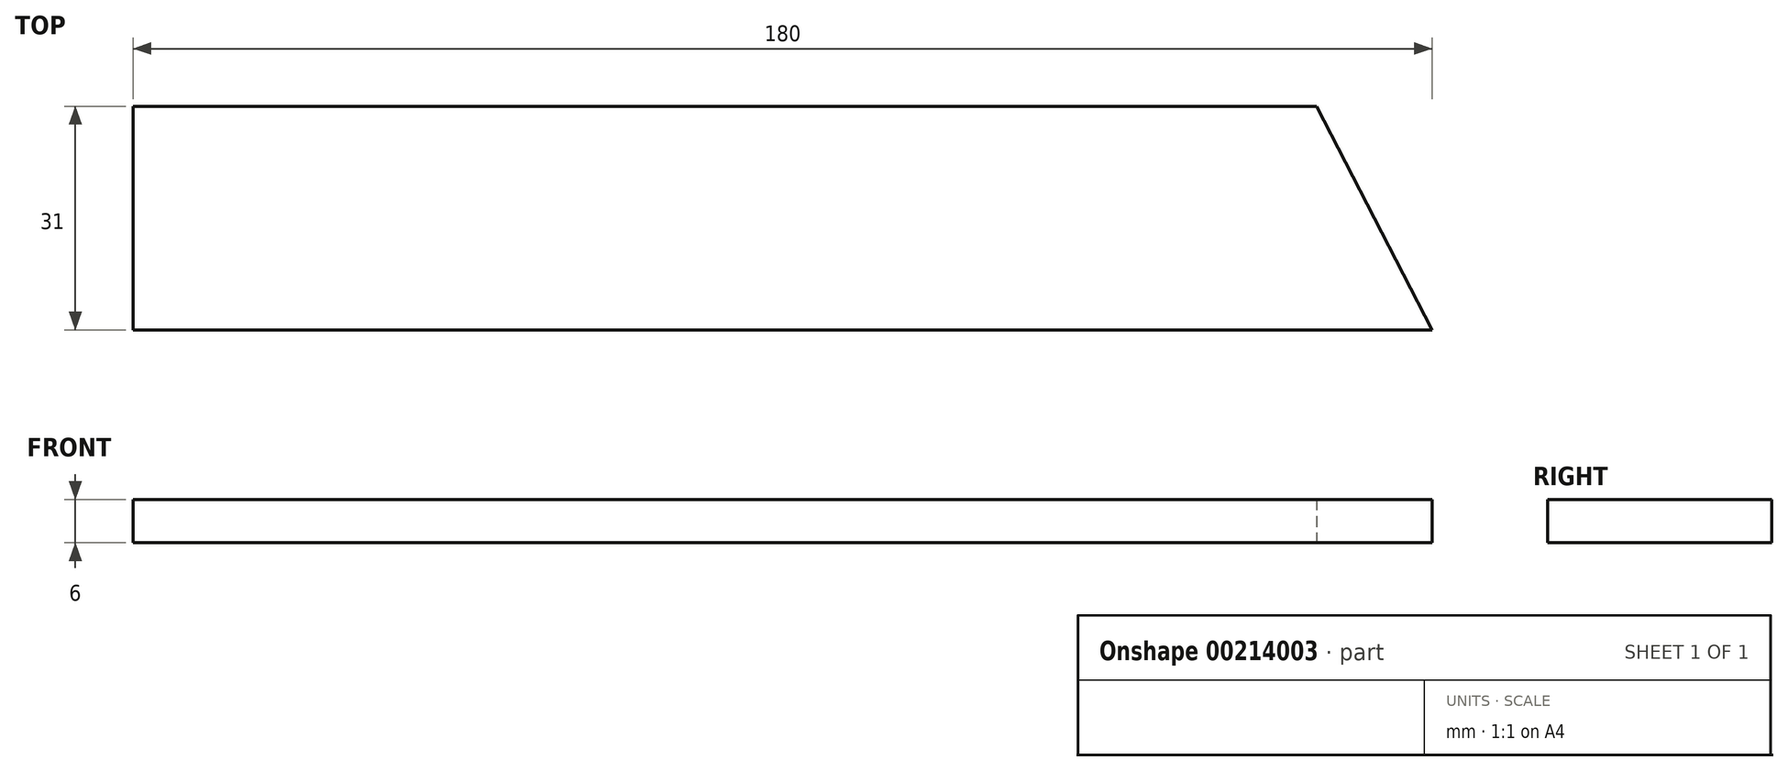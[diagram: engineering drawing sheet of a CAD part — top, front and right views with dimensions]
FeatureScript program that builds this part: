
annotation { "Feature Type Name" : "Feature", "Feature Type Description" : "" }
export const myFeature = defineFeature(function(context is Context, id is Id, definition is map)
    precondition{}
    {
        {
            var Q0;
            Q0=qCreatedBy(makeId("Top.planeOp"),FACE);
            var sketch = newSketch(context, id + "F0", { "sketchPlane" : qUnion([Q0])});
            skLineSegment(sketch, "E0", {"start": v(139.81, 48.77) * mm, "end": v(-24.19, 48.77) * mm});
            skLineSegment(sketch, "E1", {"start": v(-24.19, 48.77) * mm, "end": v(-24.19, 17.77) * mm});
            skLineSegment(sketch, "E2", {"start": v(-24.19, 17.77) * mm, "end": v(155.81, 17.77) * mm});
            skLineSegment(sketch, "E3", {"start": v(155.81, 17.77) * mm, "end": v(139.81, 48.77) * mm});
            skSolve(sketch);
        }
        {
            var Q0;
            Q0 = qSketchRegion(id + "F0", true);
            extrude(context, id + "F1", {"entities" : qUnion([Q0]), "endBound" : BoundingType.SYMMETRIC, "depth" : 6 * mm});
        }
    });
